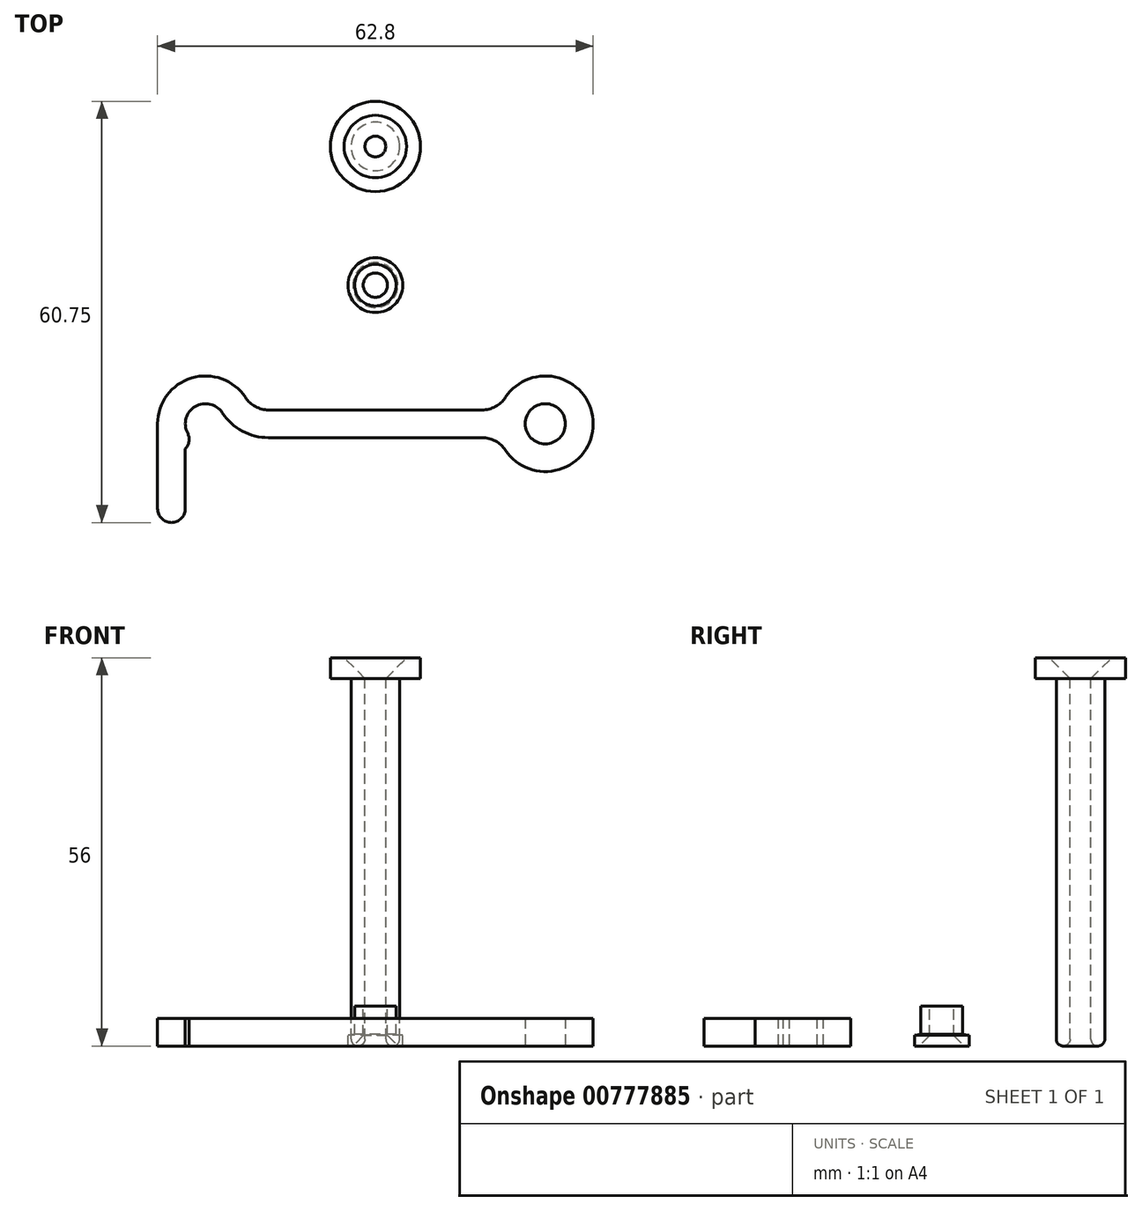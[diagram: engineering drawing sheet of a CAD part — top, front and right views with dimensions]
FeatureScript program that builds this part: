
annotation { "Feature Type Name" : "Feature", "Feature Type Description" : "" }
export const myFeature = defineFeature(function(context is Context, id is Id, definition is map)
    precondition{}
    {
        {
            assignVariable(context, id + "F0", {"name" : "thick", "anyValue" : 4});
        }
        {
            var Q0;
            Q0=qCreatedBy(makeId("Top.planeOp"),FACE);
            var sketch = newSketch(context, id + "F1", { "sketchPlane" : qUnion([Q0])});
            skCircle(sketch, "E0", {"center": v(24.5, 0) * mm, "radius": 2.9 * mm});
            skLineSegment(sketch, "E1", {"start": v(-15.4, 2) * mm, "end": v(15.4, 2) * mm});
            skLineSegment(sketch, "E2", {"start": v(-15.4, -2) * mm, "end": v(15.4, -2) * mm});
            skArc(sketch, "E3", {"start": v(-18.74, 3.8) * mm, "mid": v(-26.48, 6.6) * mm, "end": v(-31.4, 0) * mm});
            skArc(sketch, "E4", {"start": v(18.74, -3.8) * mm, "mid": v(31.4, 0) * mm, "end": v(18.74, 3.8) * mm});
            skPoint(sketch, "E5.visualSharp", {"position": v(-17.9, 2) * mm});
            skArc(sketch, "E5.filletArc", {"start": v(-18.74, 3.8) * mm, "mid": v(-17.3, 2.48) * mm, "end": v(-15.4, 2) * mm});
            skPoint(sketch, "E6.visualSharp", {"position": v(17.9, 2) * mm});
            skArc(sketch, "E6.filletArc", {"start": v(15.4, 2) * mm, "mid": v(17.3, 2.48) * mm, "end": v(18.74, 3.8) * mm});
            skPoint(sketch, "E7.visualSharp", {"position": v(17.9, -2) * mm});
            skArc(sketch, "E7.filletArc", {"start": v(18.74, -3.8) * mm, "mid": v(17.3, -2.48) * mm, "end": v(15.4, -2) * mm});
            skLineSegment(sketch, "E8", {"start": v(-38.95, 0) * mm, "end": v(-31.4, 0) * mm, "construction": true});
            skArc(sketch, "E9", {"start": v(-27.4, 0) * mm, "mid": v(-27.07, -5.83) * mm, "end": v(-26.1, -11.58) * mm, "construction": true});
            skArc(sketch, "E10", {"start": v(-15.4, -2) * mm, "mid": v(-19.2, -1.04) * mm, "end": v(-22.08, 1.6) * mm});
            skArc(sketch, "E11", {"start": v(-22.08, 1.6) * mm, "mid": v(-25.97, 2.5) * mm, "end": v(-27.08, -1.33) * mm});
            skArc(sketch, "E12", {"start": v(-27.08, -1.33) * mm, "mid": v(-23.03, -2.5) * mm, "end": v(-22.08, 1.6) * mm, "construction": true});
            skLineSegment(sketch, "E13.trimOffspring", {"start": v(-24.5, 0) * mm, "end": v(-15.4, 6) * mm, "construction": true});
            skLineSegment(sketch, "E14", {"start": v(-24.5, 0) * mm, "end": v(-37.57, -6.76) * mm, "construction": true});
            skArc(sketch, "E15.converted", {"start": v(-27.08, -1.33) * mm, "mid": v(-27.93, -4.03) * mm, "end": v(-30.63, -3.17) * mm});
            skLineSegment(sketch, "E16", {"start": v(-31.4, -12.25) * mm, "end": v(-31.4, 0) * mm});
            skArc(sketch, "E17", {"start": v(-31.4, -12.25) * mm, "mid": v(-29.4, -14.25) * mm, "end": v(-27.4, -12.25) * mm});
            skLineSegment(sketch, "E18", {"start": v(-31.4, 0) * mm, "end": v(39.35, 0) * mm, "construction": true});
            skArc(sketch, "E19", {"start": v(-31.4, 0) * mm, "mid": v(-31.2, -1.63) * mm, "end": v(-30.63, -3.17) * mm, "construction": true});
            skLineSegment(sketch, "E20", {"start": v(-27.4, -3.63) * mm, "end": v(-27.4, -12.25) * mm});
            skSolve(sketch);
        }
        {
            var Q0;
            Q0=makeQuery(id+"F1.imprint","IMPRINT",FACE,{"disambiguationData":[TD([[makeQuery(id+"F1.imprint","IMPRINT",EDGE,{"derivedFrom":sQuery(id+"F1.wireOp",EDGE,"E1")}),-1.0]])]});
            var Q1;
            {var subQ0=sQuery(id+"F1.wireOp",EDGE,"eeHx16Rx-4NO6-tVru-3ZAi-YePnJqtfmIfx");Q1=makeQuery(id+"F1.imprint","IMPRINT",FACE,{"disambiguationData":[TD([[makeQuery(id+"F1.imprint","IMPRINT",EDGE,{"derivedFrom":subQ0}),1.0]])]});}
            var Q2;
            {var subQ0=sQuery(id+"F1.wireOp",EDGE,"E15.converted");var subQ1=sQuery(id+"F1.wireOp",EDGE,"E11");var subQ2=makeQuery(id+"F1.imprint","INTERSECT",VERTEX,{"derivedFrom":[subQ1,subQ0]});Q2=makeQuery(id+"F1.imprint","IMPRINT",FACE,{"disambiguationData":[TD([[makeQuery(id+"F1.imprint","IMPRINT",EDGE,{"disambiguationData":[TD([[subQ2,1.0]])],"derivedFrom":subQ1}),-1.0]])]});}
            var Q3;
            {var subQ0=sQuery(id+"F1.wireOp",EDGE,"EOvmGg5d-Uc9d-S7nv-0y15-VxTviT8qH6WQ");Q3=makeQuery(id+"F1.imprint","IMPRINT",FACE,{"disambiguationData":[TD([[makeQuery(id+"F1.imprint","IMPRINT",EDGE,{"derivedFrom":subQ0}),1.0]])]});}
            var Q4;
            {var subQ0=sQuery(id+"F1.wireOp",EDGE,"E16");Q4=makeQuery(id+"F1.imprint","IMPRINT",FACE,{"disambiguationData":[TD([[makeQuery(id+"F1.imprint","IMPRINT",EDGE,{"derivedFrom":subQ0}),-1.0]])]});}
            extrude(context, id + "F2", {"entities" : qUnion([Q0, Q1, Q2, Q3, Q4]), "depth" : (getVariable(context, 'thick')) * mm, "offsetDistance" : 25 * mm});
        }
        {
            var Q0;
            Q0=qCreatedBy(makeId("Right.planeOp"),FACE);
            var sketch = newSketch(context, id + "F3", { "sketchPlane" : qUnion([Q0])});
            skLineSegment(sketch, "E21", {"start": v(16.05, 0) * mm, "end": v(16.05, 1.58) * mm});
            skLineSegment(sketch, "E22", {"start": v(16.05, 1.58) * mm, "end": v(17, 1.66) * mm});
            skLineSegment(sketch, "E23", {"start": v(17, 1.66) * mm, "end": v(17, 5.76) * mm});
            skLineSegment(sketch, "E24", {"start": v(17, 5.76) * mm, "end": v(18.25, 5.76) * mm});
            skLineSegment(sketch, "E25", {"start": v(18.25, 5.76) * mm, "end": v(18.25, 1.5) * mm});
            skLineSegment(sketch, "E26", {"start": v(18.25, 1.5) * mm, "end": v(16.75, 0) * mm});
            skLineSegment(sketch, "E27", {"start": v(16.75, 0) * mm, "end": v(16.05, 0) * mm});
            skLineSegment(sketch, "E28", {"start": v(20, 14.05) * mm, "end": v(20, -4.02) * mm, "construction": true});
            skLineSegment(sketch, "E29", {"start": v(36.5, 1) * mm, "end": v(36.5, 53) * mm});
            skLineSegment(sketch, "E30", {"start": v(36.5, 53) * mm, "end": v(33.5, 53) * mm});
            skLineSegment(sketch, "E31", {"start": v(33.5, 53) * mm, "end": v(33.5, 56) * mm});
            skLineSegment(sketch, "E32", {"start": v(33.5, 56) * mm, "end": v(35.5, 56) * mm});
            skLineSegment(sketch, "E33", {"start": v(35.5, 56) * mm, "end": v(38.5, 53) * mm});
            skLineSegment(sketch, "E34", {"start": v(38.5, 53) * mm, "end": v(38.5, 1) * mm});
            skLineSegment(sketch, "E35", {"start": v(40, 61.54) * mm, "end": v(40, -4.38) * mm, "construction": true});
            skArc(sketch, "E36", {"start": v(36.5, 1) * mm, "mid": v(37.5, 0) * mm, "end": v(38.5, 1) * mm});
            skSolve(sketch);
        }
        {
            var Q0;
            Q0=makeQuery(id+"F3.imprint","IMPRINT",FACE,{"disambiguationData":[TD([[makeQuery(id+"F3.imprint","IMPRINT",EDGE,{"derivedFrom":sQuery(id+"F3.wireOp",EDGE,"E21")}),-1.0]])]});
            var Q1;
            Q1=sQuery(id+"F3.wireOp",EDGE,"E28");
            revolve(context, id + "F4", {"surfaceOperationType" : NewSurfaceOperationType.NEW, "entities" : qUnion([Q0]), "axis" : qUnion([Q1]), "revolveType" : RevolveType.FULL});
        }
        {
            var Q0;
            Q0=makeQuery(id+"F3.imprint","IMPRINT",FACE,{"disambiguationData":[TD([[makeQuery(id+"F3.imprint","IMPRINT",EDGE,{"derivedFrom":sQuery(id+"F3.wireOp",EDGE,"E29")}),-1.0]])]});
            var Q1;
            Q1=sQuery(id+"F3.wireOp",EDGE,"E35");
            revolve(context, id + "F5", {"surfaceOperationType" : NewSurfaceOperationType.NEW, "entities" : qUnion([Q0]), "axis" : qUnion([Q1]), "revolveType" : RevolveType.FULL});
        }
    });
